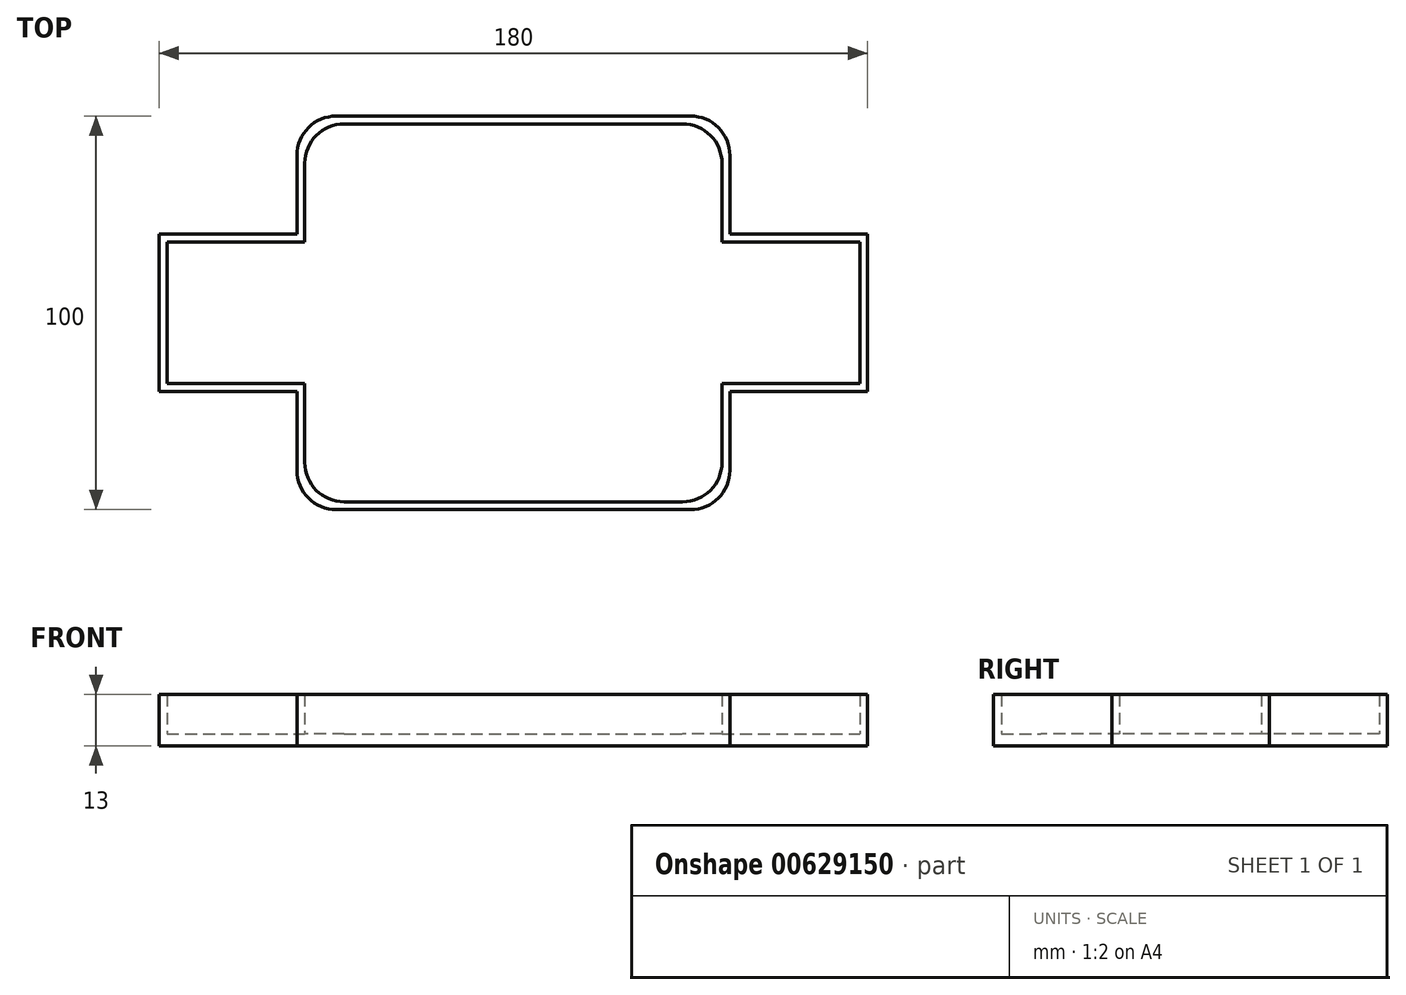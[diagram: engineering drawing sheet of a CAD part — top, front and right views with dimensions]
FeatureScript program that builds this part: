
annotation { "Feature Type Name" : "Feature", "Feature Type Description" : "" }
export const myFeature = defineFeature(function(context is Context, id is Id, definition is map)
    precondition{}
    {
        {
            var Q0;
            Q0=qCreatedBy(makeId("Top.planeOp"),FACE);
            var sketch = newSketch(context, id + "F0", { "sketchPlane" : qUnion([Q0])});
            skLineSegment(sketch, "E0.bottom", {"start": v(-55, 50) * mm, "end": v(55, 50) * mm});
            skLineSegment(sketch, "E0.top", {"start": v(-55, -50) * mm, "end": v(55, -50) * mm});
            skLineSegment(sketch, "E0.left", {"start": v(-55, 50) * mm, "end": v(-55, 20) * mm});
            skLineSegment(sketch, "E0.right", {"start": v(55, 50) * mm, "end": v(55, 20) * mm});
            skLineSegment(sketch, "E1.bottom", {"start": v(-90, 20) * mm, "end": v(-55, 20) * mm});
            skLineSegment(sketch, "E1.top", {"start": v(-90, -20) * mm, "end": v(-55, -20) * mm});
            skLineSegment(sketch, "E1.left", {"start": v(-90, 20) * mm, "end": v(-90, -20) * mm});
            skLineSegment(sketch, "E2.bottom", {"start": v(55, 20) * mm, "end": v(90, 20) * mm});
            skLineSegment(sketch, "E2.top", {"start": v(55, -20) * mm, "end": v(90, -20) * mm});
            skLineSegment(sketch, "E2.right", {"start": v(90, 20) * mm, "end": v(90, -20) * mm});
            skLineSegment(sketch, "E3.trimOffspring", {"start": v(-55, -20) * mm, "end": v(-55, -50) * mm});
            skLineSegment(sketch, "E4.trimOffspring", {"start": v(55, -20) * mm, "end": v(55, -50) * mm});
            skSolve(sketch);
        }
        {
            var Q0;
            Q0=makeQuery(id+"F0.imprint","IMPRINT",FACE,{"disambiguationData":[TD([[makeQuery(id+"F0.imprint","IMPRINT",EDGE,{"derivedFrom":sQuery(id+"F0.wireOp",EDGE,"E0.bottom")}),-1.0]])]});
            extrude(context, id + "F1", {"entities" : qUnion([Q0]), "depth" : 3 * mm, "offsetDistance" : 25 * mm});
        }
        {
            var Q0;
            Q0=makeQuery(id+"F1.opExtrude","SWEPT_EDGE",EDGE,{"disambiguationData":[OSD([sQuery(id+"F0.wireOp",EDGE,"E0.bottom"),sQuery(id+"F0.wireOp",EDGE,"E0.left")])]});
            var Q1;
            Q1=makeQuery(id+"F1.opExtrude","SWEPT_EDGE",EDGE,{"disambiguationData":[OSD([sQuery(id+"F0.wireOp",EDGE,"E0.bottom"),sQuery(id+"F0.wireOp",EDGE,"E0.right")])]});
            var Q2;
            Q2=makeQuery(id+"F1.opExtrude","SWEPT_EDGE",EDGE,{"disambiguationData":[OSD([sQuery(id+"F0.wireOp",EDGE,"E0.top"),sQuery(id+"F0.wireOp",EDGE,"E4.trimOffspring")])]});
            var Q3;
            Q3=makeQuery(id+"F1.opExtrude","SWEPT_EDGE",EDGE,{"disambiguationData":[OSD([sQuery(id+"F0.wireOp",EDGE,"E0.top"),sQuery(id+"F0.wireOp",EDGE,"E3.trimOffspring")])]});
            fillet(context, id + "F2", {"entities" : qUnion([Q0, Q1, Q2, Q3]), "radius" : 10 * mm, "tangentPropagation" : true, "allowEdgeOverflow" : false});
        }
        {
            var Q0;
            Q0=makeQuery(id+"F1.opExtrude","CAP_FACE",FACE,{"disambiguationData":[OSD([sQuery(id+"F0.wireOp",EDGE,"E0.bottom"),sQuery(id+"F0.wireOp",EDGE,"E0.top"),sQuery(id+"F0.wireOp",EDGE,"E0.left"),sQuery(id+"F0.wireOp",EDGE,"E0.right"),sQuery(id+"F0.wireOp",EDGE,"E1.bottom"),sQuery(id+"F0.wireOp",EDGE,"E1.top"),sQuery(id+"F0.wireOp",EDGE,"E1.left"),sQuery(id+"F0.wireOp",EDGE,"E2.bottom"),sQuery(id+"F0.wireOp",EDGE,"E2.top"),sQuery(id+"F0.wireOp",EDGE,"E2.right"),sQuery(id+"F0.wireOp",EDGE,"E3.trimOffspring"),sQuery(id+"F0.wireOp",EDGE,"E4.trimOffspring")])],"isStart":false});
            var sketch = newSketch(context, id + "F3", { "sketchPlane" : qUnion([Q0])});
            skLineSegment(sketch, "E5.bottom", {"start": v(-90, 20) * mm, "end": v(-55, 20) * mm});
            skLineSegment(sketch, "E5.top", {"start": v(-90, -20) * mm, "end": v(-55, -20) * mm});
            skLineSegment(sketch, "E5.left", {"start": v(-90, 20) * mm, "end": v(-90, -20) * mm});
            skLineSegment(sketch, "E5.right", {"start": v(-55, 20) * mm, "end": v(-55, -20) * mm});
            skLineSegment(sketch, "E6.bottom", {"start": v(55, 20) * mm, "end": v(90, 20) * mm});
            skLineSegment(sketch, "E6.top", {"start": v(55, -20) * mm, "end": v(90, -20) * mm});
            skLineSegment(sketch, "E6.left", {"start": v(55, 20) * mm, "end": v(55, -20) * mm});
            skLineSegment(sketch, "E6.right", {"start": v(90, 20) * mm, "end": v(90, -20) * mm});
            skLineSegment(sketch, "E7.bottom", {"start": v(-45, 50) * mm, "end": v(45, 50) * mm});
            skLineSegment(sketch, "E7.top", {"start": v(-45, -50) * mm, "end": v(45, -50) * mm});
            skLineSegment(sketch, "E7.left", {"start": v(-55, 40) * mm, "end": v(-55, -40) * mm});
            skLineSegment(sketch, "E7.right", {"start": v(55, 40) * mm, "end": v(55, -40) * mm});
            skLineSegment(sketch, "E8.bottom", {"start": v(-43, 48) * mm, "end": v(43, 48) * mm});
            skLineSegment(sketch, "E8.top", {"start": v(-43, -48) * mm, "end": v(43, -48) * mm});
            skLineSegment(sketch, "E8.left", {"start": v(-53, 38) * mm, "end": v(-53, 18) * mm});
            skLineSegment(sketch, "E8.right", {"start": v(53, 38) * mm, "end": v(53, 18) * mm});
            skLineSegment(sketch, "E9.bottom", {"start": v(53, 18) * mm, "end": v(88, 18) * mm});
            skLineSegment(sketch, "E9.top", {"start": v(53, -18) * mm, "end": v(88, -18) * mm});
            skLineSegment(sketch, "E9.right", {"start": v(88, 18) * mm, "end": v(88, -18) * mm});
            skLineSegment(sketch, "E10.bottom", {"start": v(-88, 18) * mm, "end": v(-53, 18) * mm});
            skLineSegment(sketch, "E10.top", {"start": v(-88, -18) * mm, "end": v(-53, -18) * mm});
            skLineSegment(sketch, "E10.left", {"start": v(-88, 18) * mm, "end": v(-88, -18) * mm});
            skLineSegment(sketch, "E11.trimOffspring", {"start": v(-53, -18) * mm, "end": v(-53, -38) * mm});
            skLineSegment(sketch, "E12.trimOffspring", {"start": v(53, -18) * mm, "end": v(53, -38) * mm});
            skPoint(sketch, "E13.visualSharp", {"position": v(-53, 48) * mm});
            skArc(sketch, "E13.filletArc", {"start": v(-43, 48) * mm, "mid": v(-50.07, 45.07) * mm, "end": v(-53, 38) * mm});
            skPoint(sketch, "E14.visualSharp", {"position": v(-55, 50) * mm});
            skArc(sketch, "E14.filletArc", {"start": v(-45, 50) * mm, "mid": v(-52.07, 47.07) * mm, "end": v(-55, 40) * mm});
            skPoint(sketch, "E15.visualSharp", {"position": v(53, 48) * mm});
            skArc(sketch, "E15.filletArc", {"start": v(53, 38) * mm, "mid": v(50.07, 45.07) * mm, "end": v(43, 48) * mm});
            skPoint(sketch, "E16.visualSharp", {"position": v(55, 50) * mm});
            skArc(sketch, "E16.filletArc", {"start": v(55, 40) * mm, "mid": v(52.07, 47.07) * mm, "end": v(45, 50) * mm});
            skPoint(sketch, "E17.visualSharp", {"position": v(55, -50) * mm});
            skArc(sketch, "E17.filletArc", {"start": v(45, -50) * mm, "mid": v(52.07, -47.07) * mm, "end": v(55, -40) * mm});
            skPoint(sketch, "E18.visualSharp", {"position": v(53, -48) * mm});
            skArc(sketch, "E18.filletArc", {"start": v(43, -48) * mm, "mid": v(50.07, -45.07) * mm, "end": v(53, -38) * mm});
            skPoint(sketch, "E19.visualSharp", {"position": v(-53, -48) * mm});
            skArc(sketch, "E19.filletArc", {"start": v(-53, -38) * mm, "mid": v(-50.07, -45.07) * mm, "end": v(-43, -48) * mm});
            skPoint(sketch, "E20.visualSharp", {"position": v(-55, -50) * mm});
            skArc(sketch, "E20.filletArc", {"start": v(-55, -40) * mm, "mid": v(-52.07, -47.07) * mm, "end": v(-45, -50) * mm});
            skSolve(sketch);
        }
        {
            var Q0;
            Q0 = qSketchRegion(id + "F3", true);
            extrude(context, id + "F4", {"entities" : qUnion([Q0]), "operationType" : NewBodyOperationType.ADD, "depth" : 10 * mm, "offsetDistance" : 25 * mm});
        }
    });
